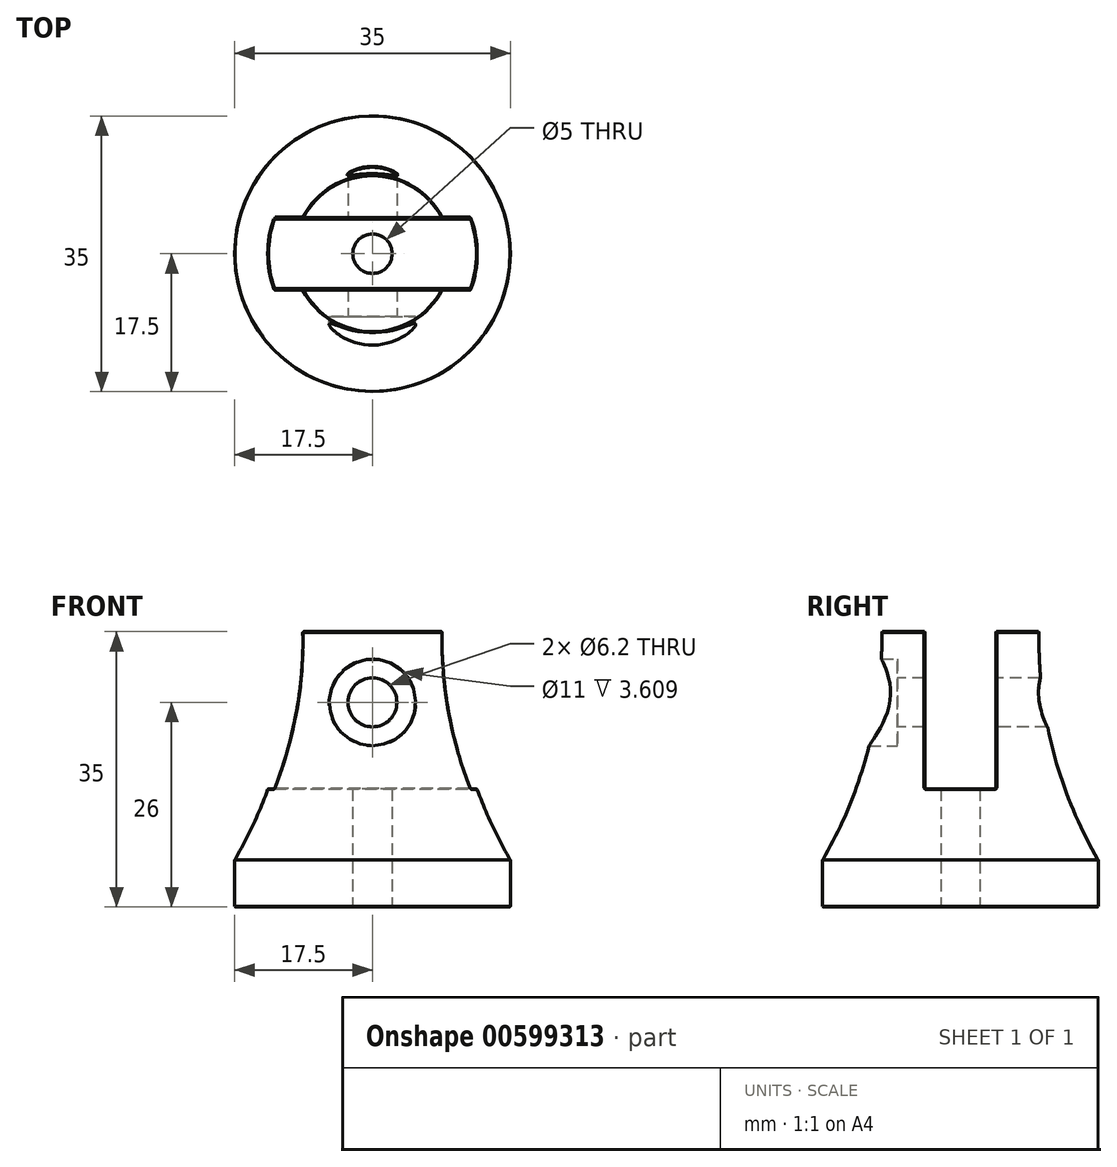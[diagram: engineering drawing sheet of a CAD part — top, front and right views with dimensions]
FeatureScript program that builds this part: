
annotation { "Feature Type Name" : "Feature", "Feature Type Description" : "" }
export const myFeature = defineFeature(function(context is Context, id is Id, definition is map)
    precondition{}
    {
        {
            var Q0;
            Q0=qCreatedBy(makeId("Front.planeOp"),FACE);
            var sketch = newSketch(context, id + "F0", { "sketchPlane" : qUnion([Q0])});
            skLineSegment(sketch, "E0", {"start": v(0, 0) * mm, "end": v(0, 35) * mm, "construction": true});
            skLineSegment(sketch, "E1", {"start": v(-17.5, 0) * mm, "end": v(-2.5, 0) * mm});
            skLineSegment(sketch, "E2", {"start": v(-2.5, 0) * mm, "end": v(-2.5, 17.5) * mm});
            skLineSegment(sketch, "E3", {"start": v(-2.5, 17.5) * mm, "end": v(0, 17.5) * mm});
            skLineSegment(sketch, "E4", {"start": v(0, 17.5) * mm, "end": v(0, 35) * mm});
            skLineSegment(sketch, "E5", {"start": v(-17.5, 0) * mm, "end": v(-17.5, 6) * mm});
            skLineSegment(sketch, "E6", {"start": v(0, 35) * mm, "end": v(-10, 35) * mm});
            skArc(sketch, "E7", {"start": v(-17.5, 6) * mm, "mid": v(-11.74, 19.98) * mm, "end": v(-10, 35) * mm});
            skSolve(sketch);
        }
        {
            var Q0;
            Q0=makeQuery(id+"F0.imprint","IMPRINT",FACE,{"disambiguationData":[TD([[makeQuery(id+"F0.imprint","IMPRINT",EDGE,{"derivedFrom":sQuery(id+"F0.wireOp",EDGE,"E1")}),1.0]])]});
            var Q1;
            Q1=sQuery(id+"F0.wireOp",EDGE,"E0");
            revolve(context, id + "F1", {"entities" : qUnion([Q0]), "axis" : qUnion([Q1]), "revolveType" : RevolveType.FULL});
        }
        {
            var Q0;
            Q0=qCreatedBy(makeId("Right.planeOp"),FACE);
            var sketch = newSketch(context, id + "F2", { "sketchPlane" : qUnion([Q0])});
            skLineSegment(sketch, "E8", {"start": v(0, 0) * mm, "end": v(0, 35) * mm, "construction": true});
            skLineSegment(sketch, "E9.bottom", {"start": v(0, 35) * mm, "end": v(-4.5, 35) * mm});
            skLineSegment(sketch, "E9.top", {"start": v(0, 15) * mm, "end": v(-4.5, 15) * mm});
            skLineSegment(sketch, "E9.left", {"start": v(0, 35) * mm, "end": v(0, 15) * mm});
            skLineSegment(sketch, "E9.right", {"start": v(-4.5, 35) * mm, "end": v(-4.5, 15) * mm});
            skLineSegment(sketch, "E10.MirrorCS", {"start": v(4.5, 35) * mm, "end": v(4.5, 15) * mm});
            skLineSegment(sketch, "E11.MirrorCS", {"start": v(0, 35) * mm, "end": v(4.5, 35) * mm});
            skLineSegment(sketch, "E12.MirrorCS", {"start": v(0, 15) * mm, "end": v(4.5, 15) * mm});
            skSolve(sketch);
        }
        {
            var Q0;
            Q0=qSketchRegion(id+"F2",true);
            extrude(context, id + "F3", {"entities" : qUnion([Q0]), "operationType" : NewBodyOperationType.REMOVE, "endBound" : BoundingType.SYMMETRIC, "oppositeDirection" : true, "depth" : 35 * mm, "offsetDistance" : 25 * mm});
        }
        {
            var Q0;
            Q0=qCreatedBy(makeId("Front.planeOp"),FACE);
            var sketch = newSketch(context, id + "F4", { "sketchPlane" : qUnion([Q0])});
            skLineSegment(sketch, "E13", {"start": v(0, 0) * mm, "end": v(0, 35) * mm, "construction": true});
            skCircle(sketch, "E14", {"center": v(0, 26) * mm, "radius": 3.1 * mm});
            skSolve(sketch);
        }
        {
            var Q0;
            Q0=makeQuery(id+"F4.imprint","IMPRINT",FACE,{"disambiguationData":[TD([[makeQuery(id+"F4.imprint","IMPRINT",EDGE,{"derivedFrom":sQuery(id+"F4.wireOp",EDGE,"E14")}),1.0]])]});
            extrude(context, id + "F5", {"entities" : qUnion([Q0]), "operationType" : NewBodyOperationType.REMOVE, "endBound" : BoundingType.SYMMETRIC, "oppositeDirection" : true, "depth" : 25 * mm, "offsetDistance" : 25 * mm});
        }
        {
            var Q0;
            Q0=makeQuery(id+"F1.opRevolve","SWEPT_FACE",FACE,{"disambiguationData":[OSD([sQuery(id+"F0.wireOp",EDGE,"E7")])]});
            var Q1;
            Q1=makeQuery(id+"F3.boolean.opBoolean","COPY",FACE,{"derivedFrom":makeQuery(id+"F3.opExtrude","SWEPT_FACE",FACE,{"disambiguationData":[OSD([sQuery(id+"F2.wireOp",EDGE,"E9.right")])]})});
            var Q2;
            Q2=makeQuery(id+"F3.boolean.opBoolean","COPY",FACE,{"derivedFrom":makeQuery(id+"F3.opExtrude","SWEPT_FACE",FACE,{"disambiguationData":[OSD([sQuery(id+"F2.wireOp",EDGE,"E10.MirrorCS")])]})});
            var Q3;
            Q3=makeQuery(id+"F1.opRevolve","SWEPT_FACE",FACE,{"disambiguationData":[OSD([sQuery(id+"F0.wireOp",EDGE,"E5")])]});
            var Q4;
            Q4=makeQuery(id+"F1.opRevolve","SWEPT_FACE",FACE,{"disambiguationData":[OSD([sQuery(id+"F0.wireOp",EDGE,"E1")])]});
            chamfer(context, id + "F6", {"entities" : qUnion([Q0, Q1, Q2, Q3, Q4]), "width" : .1 * mm, "tangentPropagation" : true});
        }
        {
            var Q0;
            Q0=qCreatedBy(makeId("Front.planeOp"),FACE);
            var sketch = newSketch(context, id + "F7", { "sketchPlane" : qUnion([Q0])});
            skCircle(sketch, "E15.0", {"center": v(0, 26) * mm, "radius": 3.1 * mm});
            skCircle(sketch, "E16", {"center": v(0, 26) * mm, "radius": 5.5 * mm});
            skSolve(sketch);
        }
        {
            var Q0;
            Q0=makeQuery(id+"F7.imprint","IMPRINT",FACE,{"disambiguationData":[TD([[makeQuery(id+"F7.imprint","IMPRINT",EDGE,{"derivedFrom":sQuery(id+"F7.wireOp",EDGE,"E15.0")}),-1.0]])]});
            var Q1;
            Q1=sQuery(id+"F7.wireOp",EDGE,"E16");
            extrude(context, id + "F8", {"entities" : qUnion([Q0]), "operationType" : NewBodyOperationType.REMOVE, "surfaceEntities" : qUnion([Q1]), "depth" : 12 * mm, "offsetDistance" : 25 * mm, "hasSecondDirection" : true, "secondDirectionOppositeDirection" : false, "secondDirectionDepth" : 8 * mm});
        }
    });
